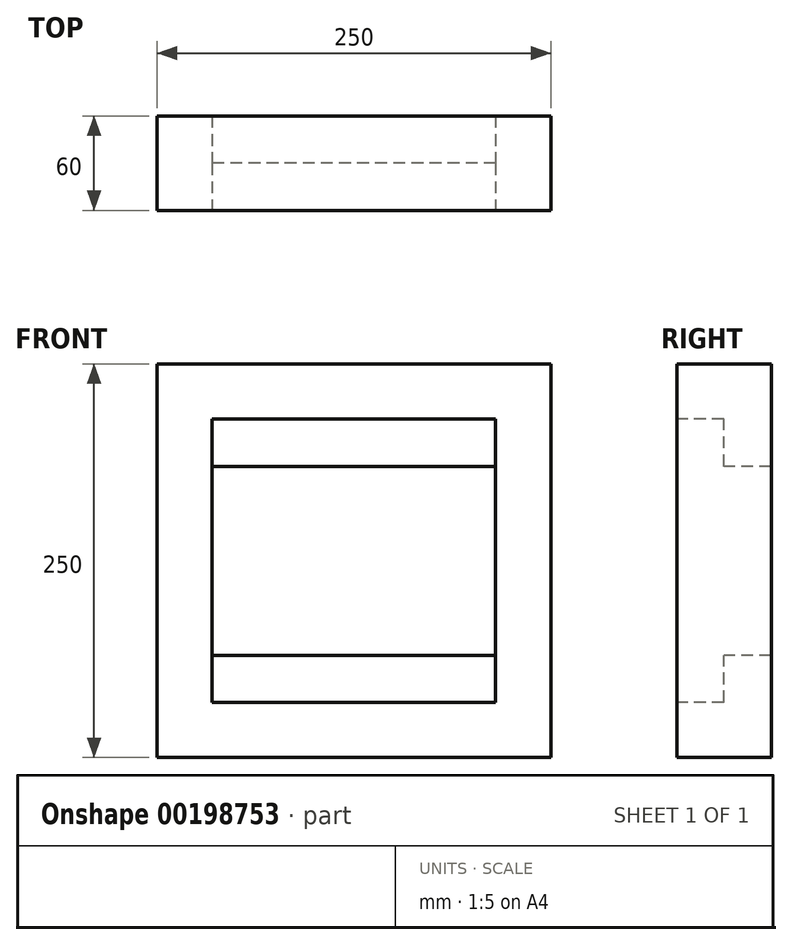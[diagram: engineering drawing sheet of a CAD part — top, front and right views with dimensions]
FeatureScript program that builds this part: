
annotation { "Feature Type Name" : "Feature", "Feature Type Description" : "" }
export const myFeature = defineFeature(function(context is Context, id is Id, definition is map)
    precondition{}
    {
        {
            var Q0;
            Q0=qCreatedBy(makeId("Right.planeOp"),FACE);
            var sketch = newSketch(context, id + "F0", { "sketchPlane" : qUnion([Q0])});
            skLineSegment(sketch, "E0.bottom", {"start": v(30, 125) * mm, "end": v(-30, 125) * mm});
            skLineSegment(sketch, "E0.top", {"start": v(30, -125) * mm, "end": v(-30, -125) * mm});
            skLineSegment(sketch, "E0.left", {"start": v(30, 125) * mm, "end": v(30, -125) * mm});
            skLineSegment(sketch, "E0.right", {"start": v(-30, 125) * mm, "end": v(-30, -125) * mm});
            skPoint(sketch, "E0.middle", {"position": v(0, 0) * mm});
            skSolve(sketch);
        }
        {
            var Q0;
            Q0 = qSketchRegion(id + "F0", true);
            extrude(context, id + "F1", {"entities" : qUnion([Q0]), "endBound" : BoundingType.SYMMETRIC, "depth" : 250 * mm});
        }
        {
            var Q0;
            Q0=makeQuery(id+"F1.opExtrude","SWEPT_FACE",FACE,{"disambiguationData":[OSD([sQuery(id+"F0.wireOp",EDGE,"E0.right")])]});
            var sketch = newSketch(context, id + "F2", { "sketchPlane" : qUnion([Q0])});
            skLineSegment(sketch, "E1.bottom", {"start": v(90, -90) * mm, "end": v(-90, -90) * mm});
            skLineSegment(sketch, "E1.top", {"start": v(90, 90) * mm, "end": v(-90, 90) * mm});
            skLineSegment(sketch, "E1.left", {"start": v(90, -90) * mm, "end": v(90, 90) * mm});
            skLineSegment(sketch, "E1.right", {"start": v(-90, -90) * mm, "end": v(-90, 90) * mm});
            skPoint(sketch, "E1.middle", {"position": v(0, 0) * mm});
            skSolve(sketch);
        }
        {
            var Q0;
            Q0 = qSketchRegion(id + "F2", true);
            extrude(context, id + "F3", {"entities" : qUnion([Q0]), "operationType" : NewBodyOperationType.REMOVE, "oppositeDirection" : true, "depth" : 30 * mm});
        }
        {
            var Q0;
            Q0=makeQuery(id+"F3.boolean.opBoolean","COPY",FACE,{"derivedFrom":makeQuery(id+"F3.opExtrude","CAP_FACE",FACE,{"disambiguationData":[OSD([sQuery(id+"F2.wireOp",EDGE,"E1.bottom"),sQuery(id+"F2.wireOp",EDGE,"E1.top"),sQuery(id+"F2.wireOp",EDGE,"E1.left"),sQuery(id+"F2.wireOp",EDGE,"E1.right")])],"isStart":false})});
            var sketch = newSketch(context, id + "F4", { "sketchPlane" : qUnion([Q0])});
            skLineSegment(sketch, "E2.bottom", {"start": v(90, -60) * mm, "end": v(-90, -60) * mm});
            skLineSegment(sketch, "E2.top", {"start": v(90, 60) * mm, "end": v(-90, 60) * mm});
            skLineSegment(sketch, "E2.left", {"start": v(90, -60) * mm, "end": v(90, 60) * mm});
            skLineSegment(sketch, "E2.right", {"start": v(-90, -60) * mm, "end": v(-90, 60) * mm});
            skPoint(sketch, "E2.middle", {"position": v(0, 0) * mm});
            skSolve(sketch);
        }
        {
            var Q0;
            Q0 = qSketchRegion(id + "F4", true);
            extrude(context, id + "F5", {"entities" : qUnion([Q0]), "operationType" : NewBodyOperationType.REMOVE, "endBound" : BoundingType.THROUGH_ALL, "oppositeDirection" : true, "depth" : 25 * mm});
        }
    });
